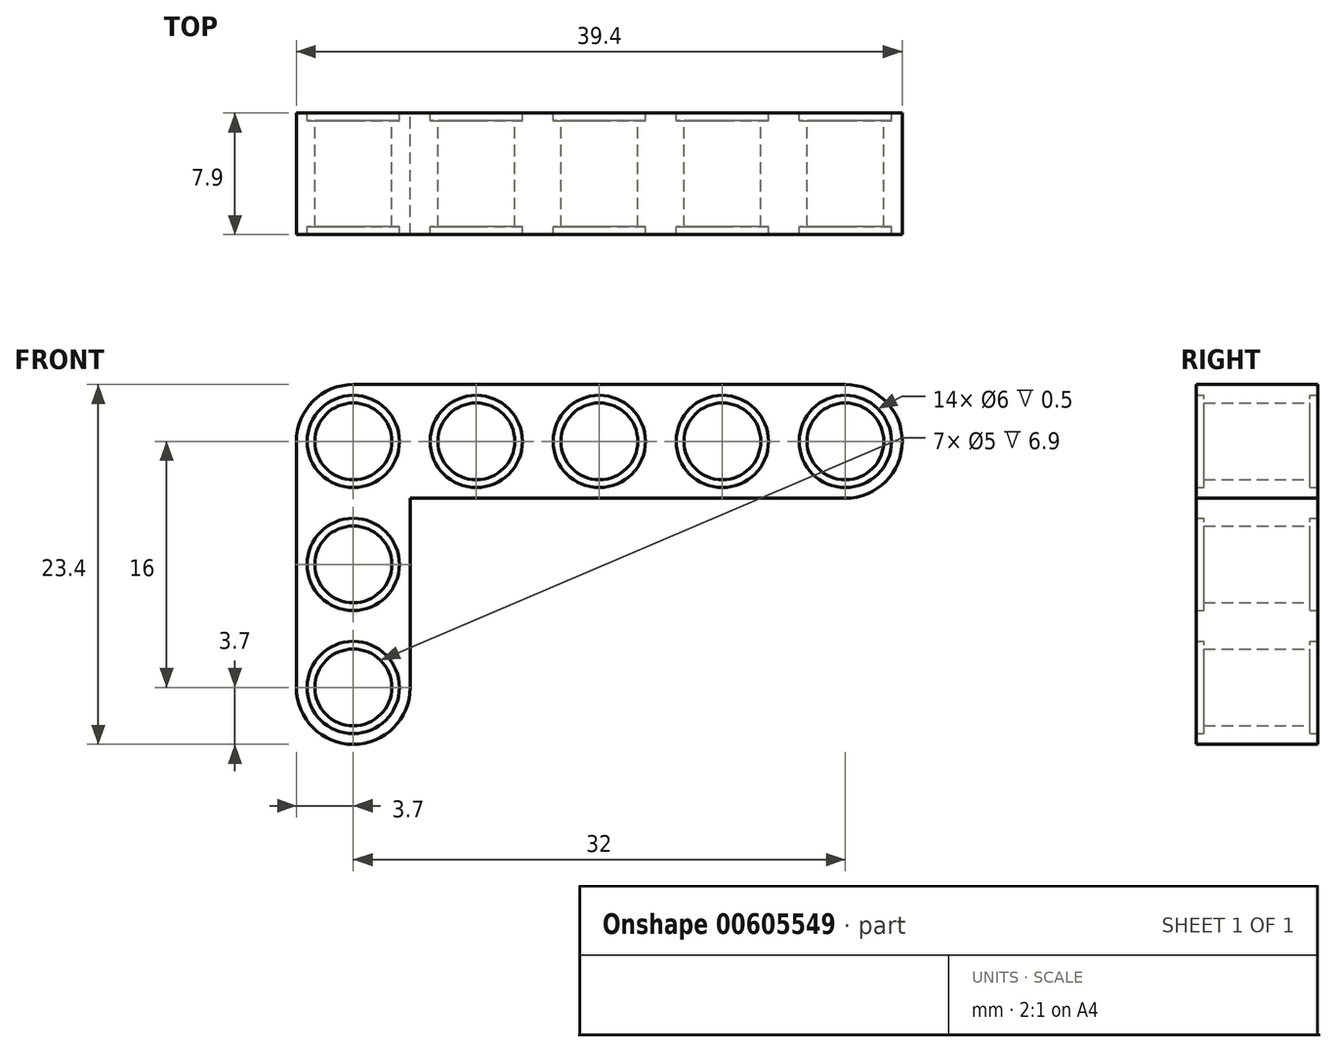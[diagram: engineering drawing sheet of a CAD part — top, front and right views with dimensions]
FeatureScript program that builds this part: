
annotation { "Feature Type Name" : "Feature", "Feature Type Description" : "" }
export const myFeature = defineFeature(function(context is Context, id is Id, definition is map)
    precondition{}
    {
        {
            var Q0;
            Q0=qCreatedBy(makeId("Front.planeOp"),FACE);
            var sketch = newSketch(context, id + "F0", { "sketchPlane" : qUnion([Q0])});
            skCircle(sketch, "E0", {"center": v(16, -3.7) * mm, "radius": 2.5 * mm});
            skCircle(sketch, "E1", {"center": v(16, -3.7) * mm, "radius": 3 * mm});
            skCircle(sketch, "E2", {"center": v(8, -3.7) * mm, "radius": 2.5 * mm});
            skCircle(sketch, "E3", {"center": v(0, -3.7) * mm, "radius": 2.5 * mm});
            skCircle(sketch, "E4", {"center": v(-8, -3.7) * mm, "radius": 2.5 * mm});
            skCircle(sketch, "E5", {"center": v(-16, -3.7) * mm, "radius": 2.5 * mm});
            skLineSegment(sketch, "E6", {"start": v(-16, -3.7) * mm, "end": v(-16, -11.7) * mm, "construction": true});
            skLineSegment(sketch, "E7", {"start": v(-16, -11.7) * mm, "end": v(-16, -19.7) * mm, "construction": true});
            skCircle(sketch, "E8", {"center": v(-16, -11.7) * mm, "radius": 2.5 * mm});
            skCircle(sketch, "E9", {"center": v(-16, -19.7) * mm, "radius": 2.5 * mm});
            skCircle(sketch, "E10", {"center": v(-16, -11.7) * mm, "radius": 3 * mm});
            skCircle(sketch, "E11", {"center": v(-16, -19.7) * mm, "radius": 3 * mm});
            skCircle(sketch, "E12", {"center": v(-16, -3.7) * mm, "radius": 3 * mm});
            skCircle(sketch, "E13", {"center": v(-8, -3.7) * mm, "radius": 3 * mm});
            skCircle(sketch, "E14", {"center": v(0, -3.7) * mm, "radius": 3 * mm});
            skCircle(sketch, "E15", {"center": v(8, -3.7) * mm, "radius": 3 * mm});
            skLineSegment(sketch, "E16", {"start": v(-19.7, 0) * mm, "end": v(-19.7, -23.4) * mm});
            skLineSegment(sketch, "E17", {"start": v(-19.7, -23.4) * mm, "end": v(-12.3, -23.4) * mm});
            skLineSegment(sketch, "E18", {"start": v(19.7, 0) * mm, "end": v(19.7, -7.4) * mm});
            skLineSegment(sketch, "E19", {"start": v(19.7, 0) * mm, "end": v(-19.7, 0) * mm});
            skLineSegment(sketch, "E20", {"start": v(19.7, -7.4) * mm, "end": v(-12.3, -7.4) * mm});
            skLineSegment(sketch, "E21", {"start": v(-12.3, -7.4) * mm, "end": v(-12.3, -23.4) * mm});
            skSolve(sketch);
        }
        {
            var Q0;
            Q0=makeQuery(id+"F0.imprint","IMPRINT",FACE,{"disambiguationData":[TD([[makeQuery(id+"F0.imprint","IMPRINT",EDGE,{"derivedFrom":sQuery(id+"F0.wireOp",EDGE,"E1")}),-1.0]])]});
            extrude(context, id + "F1", {"entities" : qUnion([Q0]), "endBound" : BoundingType.SYMMETRIC, "depth" : 7.9 * mm, "offsetDistance" : 25 * mm});
        }
        {
            var Q0;
            Q0=makeQuery(id+"F0.imprint","IMPRINT",FACE,{"disambiguationData":[TD([[makeQuery(id+"F0.imprint","IMPRINT",EDGE,{"derivedFrom":sQuery(id+"F0.wireOp",EDGE,"E0")}),-1.0]])]});
            var Q1;
            Q1=makeQuery(id+"F0.imprint","IMPRINT",FACE,{"disambiguationData":[TD([[makeQuery(id+"F0.imprint","IMPRINT",EDGE,{"derivedFrom":sQuery(id+"F0.wireOp",EDGE,"E2")}),-1.0]])]});
            var Q2;
            Q2=makeQuery(id+"F0.imprint","IMPRINT",FACE,{"disambiguationData":[TD([[makeQuery(id+"F0.imprint","IMPRINT",EDGE,{"derivedFrom":sQuery(id+"F0.wireOp",EDGE,"E3")}),-1.0]])]});
            var Q3;
            Q3=makeQuery(id+"F0.imprint","IMPRINT",FACE,{"disambiguationData":[TD([[makeQuery(id+"F0.imprint","IMPRINT",EDGE,{"derivedFrom":sQuery(id+"F0.wireOp",EDGE,"E4")}),-1.0]])]});
            var Q4;
            Q4=makeQuery(id+"F0.imprint","IMPRINT",FACE,{"disambiguationData":[TD([[makeQuery(id+"F0.imprint","IMPRINT",EDGE,{"derivedFrom":sQuery(id+"F0.wireOp",EDGE,"E5")}),-1.0]])]});
            var Q5;
            Q5=makeQuery(id+"F0.imprint","IMPRINT",FACE,{"disambiguationData":[TD([[makeQuery(id+"F0.imprint","IMPRINT",EDGE,{"derivedFrom":sQuery(id+"F0.wireOp",EDGE,"E9")}),-1.0]])]});
            var Q6;
            Q6=makeQuery(id+"F0.imprint","IMPRINT",FACE,{"disambiguationData":[TD([[makeQuery(id+"F0.imprint","IMPRINT",EDGE,{"derivedFrom":sQuery(id+"F0.wireOp",EDGE,"E8")}),-1.0]])]});
            extrude(context, id + "F2", {"entities" : qUnion([Q0, Q1, Q2, Q3, Q4, Q5, Q6]), "operationType" : NewBodyOperationType.ADD, "endBound" : BoundingType.SYMMETRIC, "depth" : 6.9 * mm, "offsetDistance" : 25 * mm});
        }
        {
            var Q0;
            Q0=makeQuery(id+"F1.opExtrude","SWEPT_EDGE",EDGE,{"disambiguationData":[OSD([sQuery(id+"F0.wireOp",EDGE,"E18"),sQuery(id+"F0.wireOp",EDGE,"E19")])]});
            var Q1;
            Q1=makeQuery(id+"F1.opExtrude","SWEPT_EDGE",EDGE,{"disambiguationData":[OSD([sQuery(id+"F0.wireOp",EDGE,"E18"),sQuery(id+"F0.wireOp",EDGE,"E20")])]});
            var Q2;
            Q2=makeQuery(id+"F1.opExtrude","SWEPT_EDGE",EDGE,{"disambiguationData":[OSD([sQuery(id+"F0.wireOp",EDGE,"E17"),sQuery(id+"F0.wireOp",EDGE,"E21")])]});
            var Q3;
            Q3=makeQuery(id+"F1.opExtrude","SWEPT_EDGE",EDGE,{"disambiguationData":[OSD([sQuery(id+"F0.wireOp",EDGE,"E16"),sQuery(id+"F0.wireOp",EDGE,"E17")])]});
            fillet(context, id + "F3", {"entities" : qUnion([Q0, Q1, Q2, Q3]), "radius" : 3.7 * mm, "tangentPropagation" : true, "allowEdgeOverflow" : false});
        }
        {
            var Q0;
            Q0=makeQuery(id+"F1.opExtrude","SWEPT_EDGE",EDGE,{"disambiguationData":[OSD([sQuery(id+"F0.wireOp",EDGE,"E16"),sQuery(id+"F0.wireOp",EDGE,"E19")])]});
            fillet(context, id + "F4", {"entities" : qUnion([Q0]), "radius" : 3.7 * mm, "tangentPropagation" : true, "allowEdgeOverflow" : false});
        }
    });
